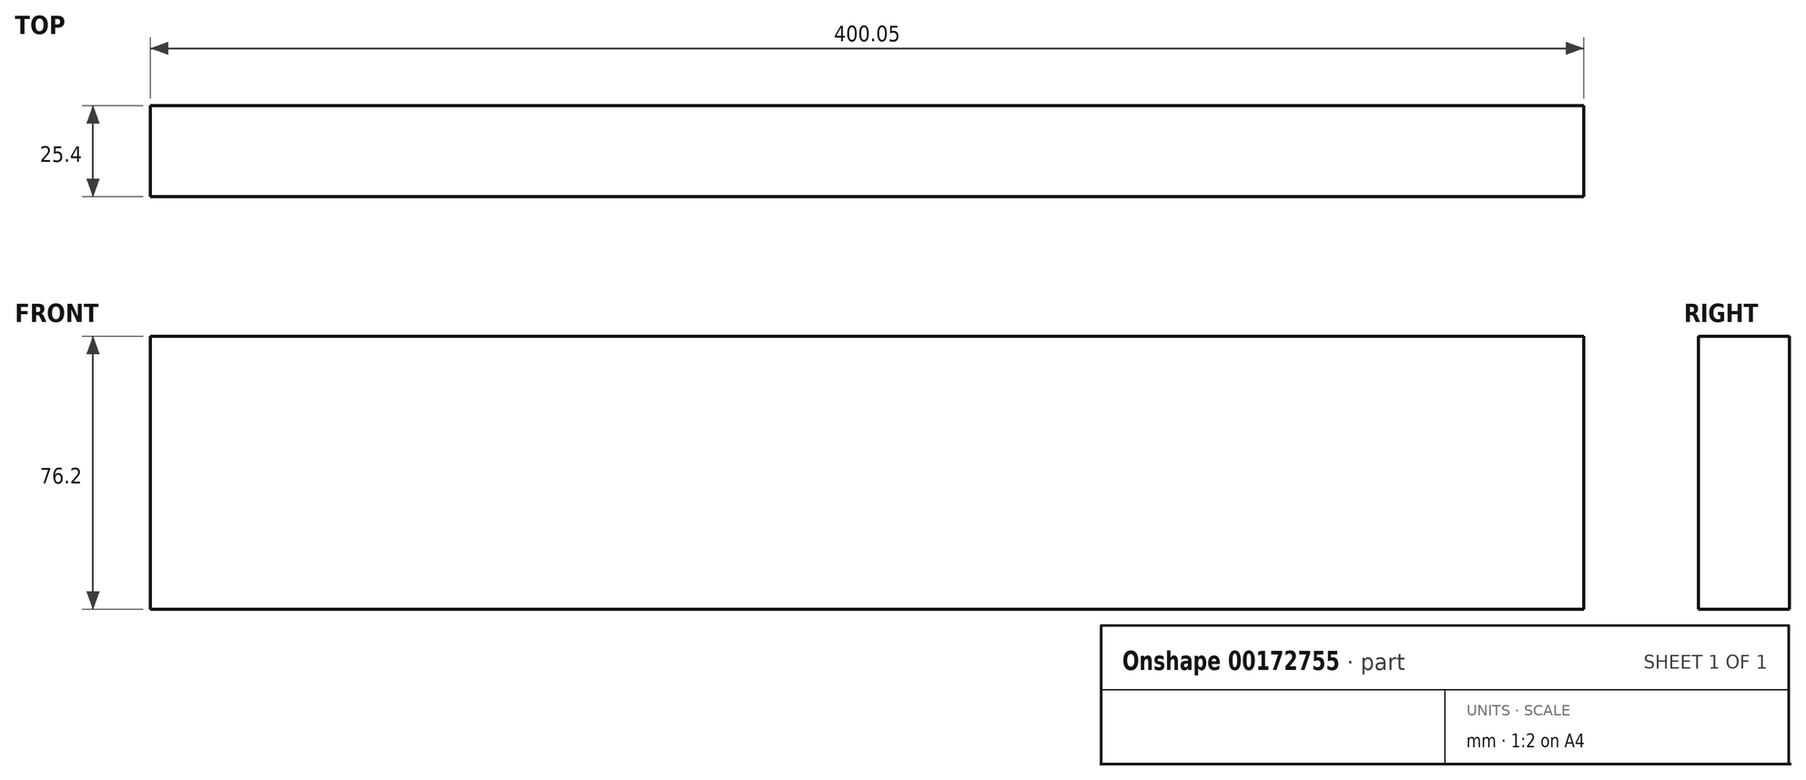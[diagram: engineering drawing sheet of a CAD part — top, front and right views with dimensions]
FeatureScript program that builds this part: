
annotation { "Feature Type Name" : "Feature", "Feature Type Description" : "" }
export const myFeature = defineFeature(function(context is Context, id is Id, definition is map)
    precondition{}
    {
        {
            var Q0;
            Q0=qCreatedBy(makeId("Front.planeOp"),FACE);
            var sketch = newSketch(context, id + "F0", { "sketchPlane" : qUnion([Q0])});
            skLineSegment(sketch, "E0.bottom", {"start": v(-209.8, 0) * mm, "end": v(190.26, 0) * mm});
            skLineSegment(sketch, "E0.top", {"start": v(-209.8, -76.2) * mm, "end": v(190.26, -76.2) * mm});
            skLineSegment(sketch, "E0.left", {"start": v(-209.8, 0) * mm, "end": v(-209.8, -76.2) * mm});
            skLineSegment(sketch, "E0.right", {"start": v(190.26, 0) * mm, "end": v(190.26, -76.2) * mm});
            skSolve(sketch);
        }
        {
            var Q0;
            Q0 = qSketchRegion(id + "F0", true);
            extrude(context, id + "F1", {"entities" : qUnion([Q0]), "depth" : 25.4 * mm});
        }
    });
